# Revit family: ASH_ArmitageShanks_MixerTaps_Contour21DeckMountedThermoMixer_A4169
name_source: partatom
category: Plumbing Fixtures
revit_build: Autodesk Revit MEP 2012 (Build: 20110309_2315(x64)
units: mm (PartAtom-declared; Revit-internal decimal feet)

## types (1)
- A4169AA Contour 21 washbasin mixer thermostatic
    AccessibilityPerformance = DDA Compliant
    Accessories = www.idealspec.co.uk
    AreaUnits = millimeters
    Assembly Code = C1030200
    AssetType = Fixed
    BIMObjectName = ASH_ArmitageShanks_MixerTaps_Contour21DeckMountedThermoMixer_A4169
    BREEAMApproved = No
    Brand = Armitage Shanks
    CWFU = 0
    Color = Chrome
    ConnectionType = Plumbing
    Cost = 0 $
    Default Elevation = 800 mm  [stored 2.62467 ft]
    Description = (tp6) contour 21 washbasin mixer thermostatic 1 hole, single sequential long lever, copper tube inlet
    DurationUnit = year
    ECA = No
    ExpectedLife = 30
    FaucetFunction = MIXED
    FaucetOperation = LEVERHANDLE
    FaucetType = PILLAR
    Features = Thermostatic single sequential long lever, copper tube inlet
    Finish = Chrome
    FlowRate = 4.6L/hr @ 3bar
    HWFU = 0
    Help = www.idealspec.co.uk/contact-us.html
    IfcExportAs = IfcValveType
    IfcExportType = FAUCET
    InstallationInstructions = www.idealspec.co.uk/resources.html
    LinearUnits = millimeters
    ManufacturerURL = www.idealspec.co.uk
    Material = Brass
    Model = A4169AA
    ModelNumber = A4169AA
    ModelReference = (TP6) Contour 21 washbasin mixer thermostatic 1 hole, single sequential long lever, copper tube inlet
    NBSDescription = Water supply fittings for wash basins and troughs
    NBSReference = 45-35-70/371
    Name = MixerTaps_Contour21-A4169_ArmitageShanks
    NettWeight = 2.85 Kg
    NominalHeight = 140 mm
    NominalLength = 123 mm
    NominalWidth = 62 mm  [stored 0.203412 ft]
    ProductInformation = www.idealspec.co.uk/assets/datasheet/A4169AA
    Shape = Sculptured
    Size = 140 x 123 x 62 mm
    Space = Internal
    SpareParts = www.fastpart-spares.co.uk
    TMV3 = Yes
    TestPressure = 10 Bar
    URL = www.idealspec.co.uk
    Uniclass2 = Pr_40_20_87_98
    ValveMechanism = Ceramic Disc Valve
    ValveOperation = Thermostatic
    Version = 2
    VolumeUnits = Litres
    WFU = 0
    WRAS = Yes
    WarrantyDescription = Manufacturers Warranty
    WarrantyDurationParts = 5
    WarrantyDurationUnit = year
    WaterEfficientProduct = No
    WorkingPressure = 3 Bar

note: [stored X ft] marks values corroborated as IEEE doubles in the binary element streams (Revit-internal decimal feet)

## geometry (parser evidence)
native form markers: Blend x2, Sweep x3
no freeform markers — native parametric forms only
